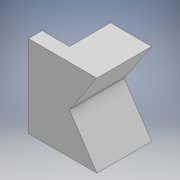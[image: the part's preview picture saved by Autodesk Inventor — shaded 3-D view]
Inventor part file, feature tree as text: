
AUTODESK INVENTOR PART (.ipt)
format: ipt  version: 2018 (Build 220112000, 112)  size: 121,344 bytes
history: native  units: mm
features: extrude x4, sketch x3
ambient origin geometry x8: Origin, YZ Plane, XZ Plane, XY Plane, X Axis, Y Axis, Z Axis, Center Point
bodies: Solid1 (feature_tree)
feature tree (7):
  sketch  "Sketch3"  dims[d12=25.0mm d13=5.0mm]
  extrude  "Extrusion1"  Depth=5.0mm
  extrude  "Extrusion2"  Depth=15.0mm
  extrude  "Extrusion4"  Depth=15.0mm TaperAngle=0.0deg
  extrude  "Extrusion5"  Depth=10.0mm
  sketch  "Sketch5"  dims[d14=10.0mm d15=15.0mm]
  sketch  "Sketch6"  dims[d16=15.0mm d17=15.0mm d18=0.0mm d19=10.0mm d20=15.0mm d21=0.0mm d24=10.0mm d25=10.0mm d26=20.0mm d27=0.0mm d28=10.0mm d29=0.0mm]
